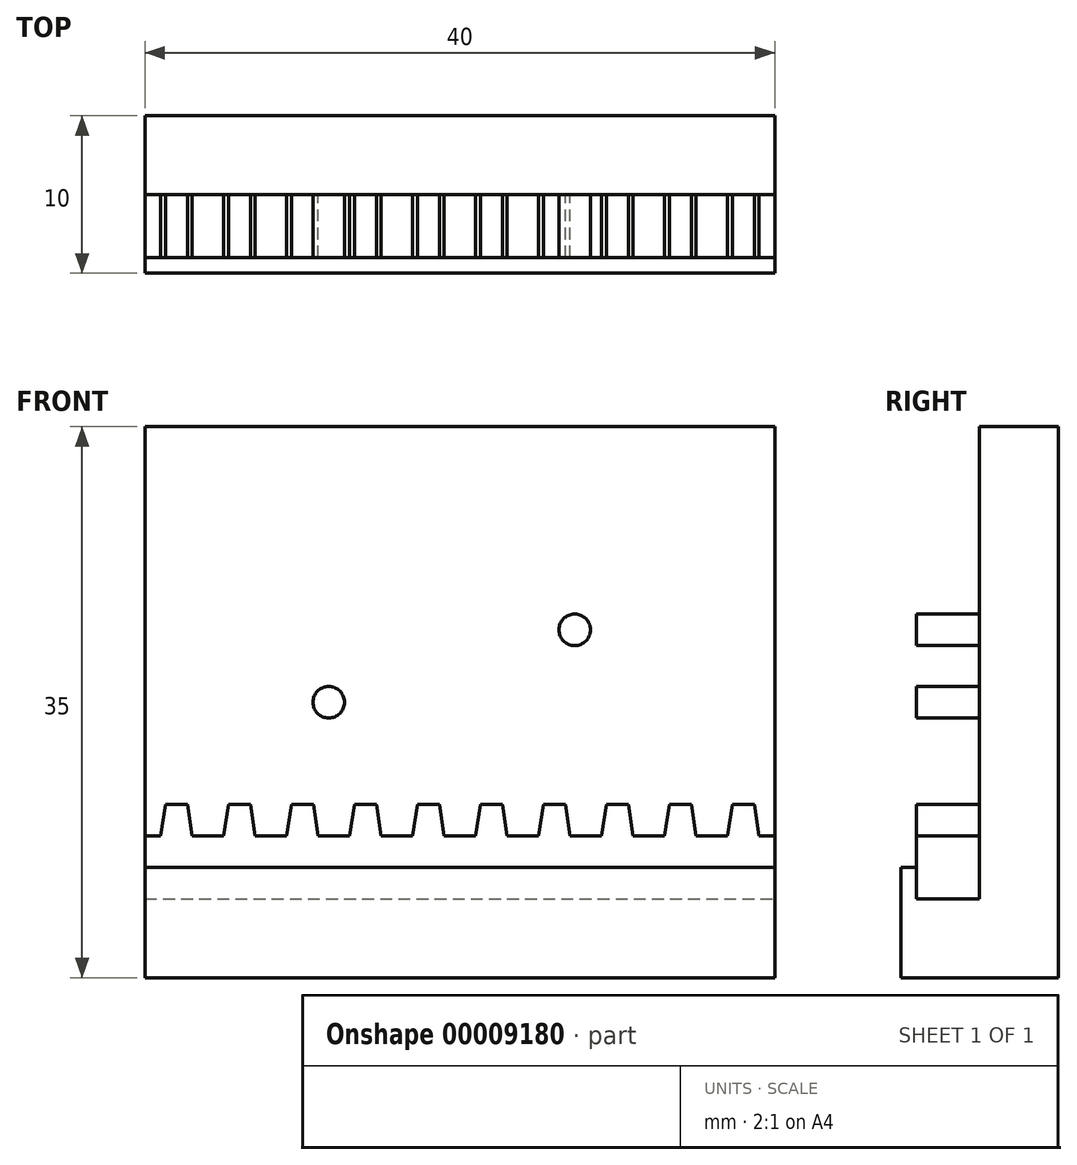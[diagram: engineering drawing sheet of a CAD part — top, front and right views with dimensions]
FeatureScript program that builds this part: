
annotation { "Feature Type Name" : "Feature", "Feature Type Description" : "" }
export const myFeature = defineFeature(function(context is Context, id is Id, definition is map)
    precondition{}
    {
        {
            var Q0;
            Q0=qCreatedBy(makeId("Front.planeOp"),FACE);
            var sketch = newSketch(context, id + "F0", { "sketchPlane" : qUnion([Q0])});
            skLineSegment(sketch, "E0.rect.bottom", {"start": v(-20, 17.5) * mm, "end": v(20, 17.5) * mm});
            skLineSegment(sketch, "E0.rect.top", {"start": v(-20, -17.5) * mm, "end": v(20, -17.5) * mm});
            skLineSegment(sketch, "E0.rect.left", {"start": v(-20, 17.5) * mm, "end": v(-20, -17.5) * mm});
            skLineSegment(sketch, "E0.rect.right", {"start": v(20, 17.5) * mm, "end": v(20, -17.5) * mm});
            skPoint(sketch, "E0.rect.middle", {"position": v(0, 0) * mm});
            skSolve(sketch);
        }
        {
            var Q0;
            Q0 = qSketchRegion(id + "F0", true);
            extrude(context, id + "F1", {"entities" : qUnion([Q0]), "depth" : 10 * mm});
        }
        {
            var Q0;
            Q0=makeQuery(id+"F1.opExtrude","CAP_FACE",FACE,{"disambiguationData":[OSD([sQuery(id+"F0.wireOp",EDGE,"E0.rect.bottom"),sQuery(id+"F0.wireOp",EDGE,"E0.rect.top"),sQuery(id+"F0.wireOp",EDGE,"E0.rect.left"),sQuery(id+"F0.wireOp",EDGE,"E0.rect.right")])],"isStart":false});
            var sketch = newSketch(context, id + "F2", { "sketchPlane" : qUnion([Q0])});
            skLineSegment(sketch, "E1.bottom", {"start": v(-20, 17.5) * mm, "end": v(20, 17.5) * mm});
            skLineSegment(sketch, "E1.top", {"start": v(-20, -12.5) * mm, "end": v(20, -12.5) * mm});
            skLineSegment(sketch, "E1.left", {"start": v(-20, 17.5) * mm, "end": v(-20, -12.5) * mm});
            skLineSegment(sketch, "E1.right", {"start": v(20, 17.5) * mm, "end": v(20, -12.5) * mm});
            skSolve(sketch);
        }
        {
            var Q0;
            Q0 = qSketchRegion(id + "F2", true);
            extrude(context, id + "F3", {"entities" : qUnion([Q0]), "operationType" : NewBodyOperationType.REMOVE, "oppositeDirection" : true, "depth" : 5 * mm});
        }
        {
            var Q0;
            Q0=makeQuery(id+"F1.opExtrude","SWEPT_FACE",FACE,{"disambiguationData":[OSD([sQuery(id+"F0.wireOp",EDGE,"E0.rect.right")])]});
            var sketch = newSketch(context, id + "F4", { "sketchPlane" : qUnion([Q0])});
            skLineSegment(sketch, "E2.bottom", {"start": v(-10, -12.5) * mm, "end": v(-9, -12.5) * mm});
            skLineSegment(sketch, "E2.top", {"start": v(-10, -10.5) * mm, "end": v(-9, -10.5) * mm});
            skLineSegment(sketch, "E2.left", {"start": v(-10, -12.5) * mm, "end": v(-10, -10.5) * mm});
            skLineSegment(sketch, "E2.right", {"start": v(-9, -12.5) * mm, "end": v(-9, -10.5) * mm});
            skSolve(sketch);
        }
        {
            var Q0;
            Q0 = qSketchRegion(id + "F4", true);
            var Q1;
            Q1=makeQuery(id+"F1.opExtrude","SWEPT_FACE",FACE,{"disambiguationData":[OSD([sQuery(id+"F0.wireOp",EDGE,"E0.rect.left")])]});
            extrude(context, id + "F5", {"entities" : qUnion([Q0]), "operationType" : NewBodyOperationType.ADD, "endBound" : BoundingType.UP_TO_SURFACE, "oppositeDirection" : true, "endBoundEntityFace" : qUnion([Q1]), "depth" : 25 * mm});
        }
        {
            var Q0;
            Q0=makeQuery(id+"F3.boolean.opBoolean","COPY",FACE,{"derivedFrom":makeQuery(id+"F3.opExtrude","CAP_FACE",FACE,{"disambiguationData":[OSD([sQuery(id+"F2.wireOp",EDGE,"E1.bottom"),sQuery(id+"F2.wireOp",EDGE,"E1.top"),sQuery(id+"F2.wireOp",EDGE,"E1.left"),sQuery(id+"F2.wireOp",EDGE,"E1.right")])],"isStart":false})});
            var sketch = newSketch(context, id + "F6", { "sketchPlane" : qUnion([Q0])});
            skCircle(sketch, "E3", {"center": v(7.3, 4.6) * mm, "radius": 1 * mm});
            skCircle(sketch, "E4", {"center": v(-8.33, 0) * mm, "radius": 1 * mm});
            skSolve(sketch);
        }
        {
            var Q0;
            Q0 = qSketchRegion(id + "F6", true);
            extrude(context, id + "F7", {"entities" : qUnion([Q0]), "operationType" : NewBodyOperationType.ADD, "depth" : 4 * mm});
        }
        {
            var Q0;
            Q0=makeQuery(id+"F3.boolean.opBoolean","COPY",FACE,{"derivedFrom":makeQuery(id+"F3.opExtrude","CAP_FACE",FACE,{"disambiguationData":[OSD([sQuery(id+"F2.wireOp",EDGE,"E1.bottom"),sQuery(id+"F2.wireOp",EDGE,"E1.top"),sQuery(id+"F2.wireOp",EDGE,"E1.left"),sQuery(id+"F2.wireOp",EDGE,"E1.right")])],"isStart":false})});
            var sketch = newSketch(context, id + "F8", { "sketchPlane" : qUnion([Q0])});
            skLineSegment(sketch, "E5.bottom", {"start": v(-20, -12.5) * mm, "end": v(20, -12.5) * mm});
            skLineSegment(sketch, "E5.top", {"start": v(-20, -8.5) * mm, "end": v(20, -8.5) * mm});
            skLineSegment(sketch, "E5.left", {"start": v(-20, -12.5) * mm, "end": v(-20, -8.5) * mm});
            skLineSegment(sketch, "E5.right", {"start": v(20, -12.5) * mm, "end": v(20, -8.5) * mm});
            skLineSegment(sketch, "E6", {"start": v(-18, -8.5) * mm, "end": v(-18, -12.5) * mm, "construction": true});
            skLineSegment(sketch, "E7", {"start": v(-19, -8.5) * mm, "end": v(-18.7, -6.5) * mm});
            skLineSegment(sketch, "E8", {"start": v(-18.7, -6.5) * mm, "end": v(-18, -6.5) * mm});
            skLineSegment(sketch, "E9.MirrorCS", {"start": v(-17, -8.5) * mm, "end": v(-17.3, -6.5) * mm});
            skLineSegment(sketch, "E10.MirrorCS", {"start": v(-17.3, -6.5) * mm, "end": v(-18, -6.5) * mm});
            skLineSegment(sketch, "E11.1.0.0", {"start": v(-15, -8.5) * mm, "end": v(-14.7, -6.5) * mm});
            skLineSegment(sketch, "E11.1.0.1", {"start": v(-14.7, -6.5) * mm, "end": v(-14, -6.5) * mm});
            skLineSegment(sketch, "E11.1.0.2", {"start": v(-13.3, -6.5) * mm, "end": v(-14, -6.5) * mm});
            skLineSegment(sketch, "E11.1.0.3", {"start": v(-13, -8.5) * mm, "end": v(-13.3, -6.5) * mm});
            skLineSegment(sketch, "E11.2.0.0", {"start": v(-11, -8.5) * mm, "end": v(-10.7, -6.5) * mm});
            skLineSegment(sketch, "E11.2.0.1", {"start": v(-10.7, -6.5) * mm, "end": v(-10, -6.5) * mm});
            skLineSegment(sketch, "E11.2.0.2", {"start": v(-9.3, -6.5) * mm, "end": v(-10, -6.5) * mm});
            skLineSegment(sketch, "E11.2.0.3", {"start": v(-9, -8.5) * mm, "end": v(-9.3, -6.5) * mm});
            skLineSegment(sketch, "E11.3.0.0", {"start": v(-7, -8.5) * mm, "end": v(-6.7, -6.5) * mm});
            skLineSegment(sketch, "E11.3.0.1", {"start": v(-6.7, -6.5) * mm, "end": v(-6, -6.5) * mm});
            skLineSegment(sketch, "E11.3.0.2", {"start": v(-5.3, -6.5) * mm, "end": v(-6, -6.5) * mm});
            skLineSegment(sketch, "E11.3.0.3", {"start": v(-5, -8.5) * mm, "end": v(-5.3, -6.5) * mm});
            skLineSegment(sketch, "E11.4.0.0", {"start": v(-3, -8.5) * mm, "end": v(-2.7, -6.5) * mm});
            skLineSegment(sketch, "E11.4.0.1", {"start": v(-2.7, -6.5) * mm, "end": v(-2, -6.5) * mm});
            skLineSegment(sketch, "E11.4.0.2", {"start": v(-1.3, -6.5) * mm, "end": v(-2, -6.5) * mm});
            skLineSegment(sketch, "E11.4.0.3", {"start": v(-1, -8.5) * mm, "end": v(-1.3, -6.5) * mm});
            skLineSegment(sketch, "E11.5.0.0", {"start": v(1, -8.5) * mm, "end": v(1.3, -6.5) * mm});
            skLineSegment(sketch, "E11.5.0.1", {"start": v(1.3, -6.5) * mm, "end": v(2, -6.5) * mm});
            skLineSegment(sketch, "E11.5.0.2", {"start": v(2.7, -6.5) * mm, "end": v(2, -6.5) * mm});
            skLineSegment(sketch, "E11.5.0.3", {"start": v(3, -8.5) * mm, "end": v(2.7, -6.5) * mm});
            skLineSegment(sketch, "E11.6.0.0", {"start": v(5, -8.5) * mm, "end": v(5.3, -6.5) * mm});
            skLineSegment(sketch, "E11.6.0.1", {"start": v(5.3, -6.5) * mm, "end": v(6, -6.5) * mm});
            skLineSegment(sketch, "E11.6.0.2", {"start": v(6.7, -6.5) * mm, "end": v(6, -6.5) * mm});
            skLineSegment(sketch, "E11.6.0.3", {"start": v(7, -8.5) * mm, "end": v(6.7, -6.5) * mm});
            skLineSegment(sketch, "E11.7.0.0", {"start": v(9, -8.5) * mm, "end": v(9.3, -6.5) * mm});
            skLineSegment(sketch, "E11.7.0.1", {"start": v(9.3, -6.5) * mm, "end": v(10, -6.5) * mm});
            skLineSegment(sketch, "E11.7.0.2", {"start": v(10.7, -6.5) * mm, "end": v(10, -6.5) * mm});
            skLineSegment(sketch, "E11.7.0.3", {"start": v(11, -8.5) * mm, "end": v(10.7, -6.5) * mm});
            skLineSegment(sketch, "E11.8.0.0", {"start": v(13, -8.5) * mm, "end": v(13.3, -6.5) * mm});
            skLineSegment(sketch, "E11.8.0.1", {"start": v(13.3, -6.5) * mm, "end": v(14, -6.5) * mm});
            skLineSegment(sketch, "E11.8.0.2", {"start": v(14.7, -6.5) * mm, "end": v(14, -6.5) * mm});
            skLineSegment(sketch, "E11.8.0.3", {"start": v(15, -8.5) * mm, "end": v(14.7, -6.5) * mm});
            skLineSegment(sketch, "E11.9.0.0", {"start": v(17, -8.5) * mm, "end": v(17.3, -6.5) * mm});
            skLineSegment(sketch, "E11.9.0.1", {"start": v(17.3, -6.5) * mm, "end": v(18, -6.5) * mm});
            skLineSegment(sketch, "E11.9.0.2", {"start": v(18.7, -6.5) * mm, "end": v(18, -6.5) * mm});
            skLineSegment(sketch, "E11.9.0.3", {"start": v(19, -8.5) * mm, "end": v(18.7, -6.5) * mm});
            skLineSegment(sketch, "E11.direction1", {"start": v(-19, -8.5) * mm, "end": v(-15, -8.5) * mm, "construction": true});
            skSolve(sketch);
        }
        {
            var Q0;
            Q0 = qSketchRegion(id + "F8", true);
            extrude(context, id + "F9", {"entities" : qUnion([Q0]), "depth" : 4 * mm});
        }
    });
